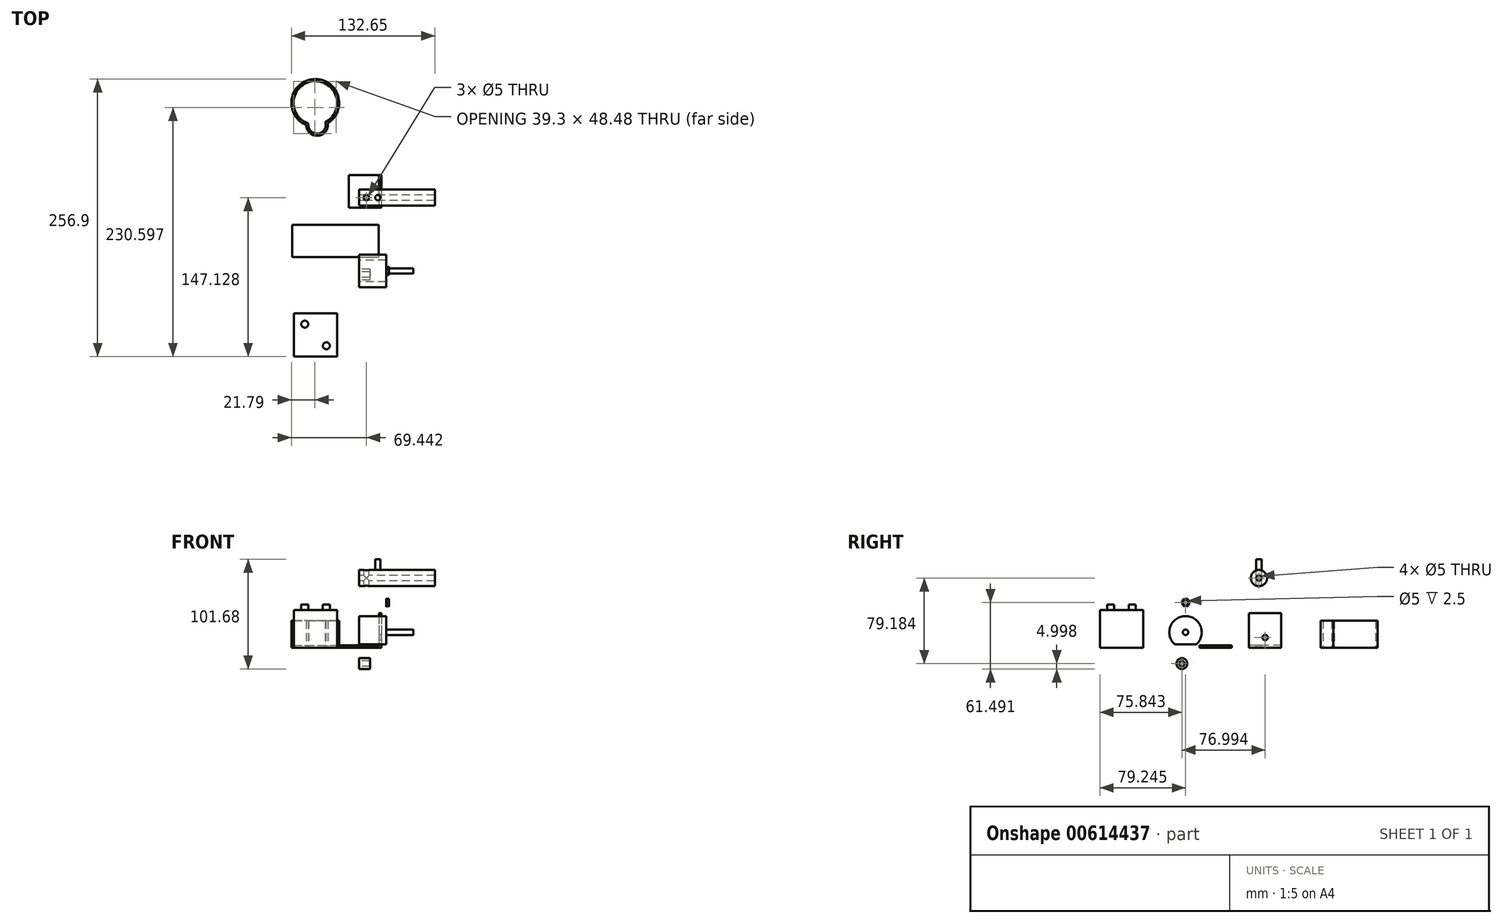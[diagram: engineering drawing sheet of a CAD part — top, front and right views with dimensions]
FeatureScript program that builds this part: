
annotation { "Feature Type Name" : "Feature", "Feature Type Description" : "" }
export const myFeature = defineFeature(function(context is Context, id is Id, definition is map)
    precondition{}
    {
        {
            var Q0;
            Q0=qCreatedBy(makeId("Top.planeOp"),FACE);
            var sketch = newSketch(context, id + "F0", { "sketchPlane" : qUnion([Q0])});
            skLineSegment(sketch, "E0.bottom", {"start": v(-9.51, 45.78) * mm, "end": v(20.49, 45.78) * mm});
            skLineSegment(sketch, "E0.top", {"start": v(-9.51, 15.78) * mm, "end": v(20.49, 15.78) * mm});
            skLineSegment(sketch, "E0.left", {"start": v(-9.51, 45.78) * mm, "end": v(-9.51, 15.78) * mm});
            skLineSegment(sketch, "E0.right", {"start": v(20.49, 45.78) * mm, "end": v(20.49, 15.78) * mm});
            skLineSegment(sketch, "E1.bottom", {"start": v(-61.86, 0) * mm, "end": v(18.14, 0) * mm});
            skLineSegment(sketch, "E1.top", {"start": v(-61.86, -30) * mm, "end": v(18.14, -30) * mm});
            skLineSegment(sketch, "E1.left", {"start": v(-61.86, 0) * mm, "end": v(-61.86, -30) * mm});
            skLineSegment(sketch, "E1.right", {"start": v(18.14, 0) * mm, "end": v(18.14, -30) * mm});
            skArc(sketch, "E2", {"start": v(-48.93, 92.28) * mm, "mid": v(-38.15, 82.3) * mm, "end": v(-29.06, 93.85) * mm});
            skArc(sketch, "E3", {"start": v(-29.06, 93.85) * mm, "mid": v(-42.29, 134.77) * mm, "end": v(-48.93, 92.28) * mm});
            skArc(sketch, "E4", {"start": v(-31.36, 94.85) * mm, "mid": v(-42.13, 132.78) * mm, "end": v(-46.82, 93.63) * mm});
            skArc(sketch, "E5", {"start": v(-46.82, 93.63) * mm, "mid": v(-38.3, 84.3) * mm, "end": v(-31.36, 94.85) * mm});
            skLineSegment(sketch, "E6.bottom", {"start": v(-60.3, -82.06) * mm, "end": v(-20.3, -82.06) * mm});
            skLineSegment(sketch, "E6.top", {"start": v(-60.3, -122.06) * mm, "end": v(-20.3, -122.06) * mm});
            skLineSegment(sketch, "E6.left", {"start": v(-60.3, -82.06) * mm, "end": v(-60.3, -122.06) * mm});
            skLineSegment(sketch, "E6.right", {"start": v(-20.3, -82.06) * mm, "end": v(-20.3, -122.06) * mm});
            skSolve(sketch);
        }
        {
            var Q0;
            Q0=makeQuery(id+"F0.imprint","IMPRINT",FACE,{"disambiguationData":[TD([[makeQuery(id+"F0.imprint","IMPRINT",EDGE,{"derivedFrom":sQuery(id+"F0.wireOp",EDGE,"E0.bottom")}),-1.0]])]});
            extrude(context, id + "F1", {"entities" : qUnion([Q0]), "depth" : 2 * mm, "offsetDistance" : 25 * mm});
        }
        {
            var Q0;
            Q0=makeQuery(id+"F1.opExtrude","CAP_FACE",FACE,{"disambiguationData":[OSD([sQuery(id+"F0.wireOp",EDGE,"E0.bottom"),sQuery(id+"F0.wireOp",EDGE,"E0.top"),sQuery(id+"F0.wireOp",EDGE,"E0.left"),sQuery(id+"F0.wireOp",EDGE,"E0.right")])],"isStart":false});
            var sketch = newSketch(context, id + "F2", { "sketchPlane" : qUnion([Q0])});
            skLineSegment(sketch, "E7", {"start": v(18.49, 45.78) * mm, "end": v(18.49, 15.78) * mm});
            skSolve(sketch);
        }
        {
            var Q0;
            {var subQ0=sQuery(id+"F2.wireOp",EDGE,"E7");Q0=makeQuery(id+"F2.imprint","IMPRINT",FACE,{"disambiguationData":[TD([[makeQuery(id+"F2.imprint","IMPRINT",EDGE,{"derivedFrom":subQ0}),1.0]])]});}
            extrude(context, id + "F3", {"entities" : qUnion([Q0]), "operationType" : NewBodyOperationType.ADD, "depth" : 30 * mm, "offsetDistance" : 25 * mm});
        }
        {
            var Q0;
            Q0=qCreatedBy(makeId("Right.planeOp"),FACE);
            var sketch = newSketch(context, id + "F4", { "sketchPlane" : qUnion([Q0])});
            skArc(sketch, "E8", {"start": v(-32.74, 3.14) * mm, "mid": v(-42.82, 29.25) * mm, "end": v(-52.9, 3.14) * mm});
            skLineSegment(sketch, "E9", {"start": v(-52.9, 3.14) * mm, "end": v(-32.74, 3.14) * mm});
            skCircle(sketch, "E10", {"center": v(-46.22, -14.73) * mm, "radius": 2.5 * mm});
            skCircle(sketch, "E11", {"center": v(-46.22, -14.73) * mm, "radius": 5 * mm});
            skCircle(sketch, "E12", {"center": v(-15.18, -14.73) * mm, "radius": 2.5 * mm});
            skCircle(sketch, "E13", {"center": v(-15.18, -14.73) * mm, "radius": 3.75 * mm});
            skSolve(sketch);
        }
        {
            var Q0;
            Q0=makeQuery(id+"F4.imprint","IMPRINT",FACE,{"disambiguationData":[TD([[makeQuery(id+"F4.imprint","IMPRINT",EDGE,{"derivedFrom":sQuery(id+"F4.wireOp",EDGE,"E8")}),1.0]])]});
            extrude(context, id + "F5", {"entities" : qUnion([Q0]), "depth" : 25 * mm, "offsetDistance" : 25 * mm});
        }
        {
            var Q0;
            Q0=makeQuery(id+"F5.opExtrude","CAP_FACE",FACE,{"disambiguationData":[OSD([sQuery(id+"F4.wireOp",EDGE,"E8"),sQuery(id+"F4.wireOp",EDGE,"E9")])],"isStart":false});
            var sketch = newSketch(context, id + "F6", { "sketchPlane" : qUnion([Q0])});
            skCircle(sketch, "E14", {"center": v(-42.82, 14.25) * mm, "radius": 2.5 * mm});
            skArc(sketch, "E15", {"start": v(-41.34, 45.21) * mm, "mid": v(-41.43, 45.25) * mm, "end": v(-41.52, 45.28) * mm});
            skCircle(sketch, "E16", {"center": v(-42.82, 41.76) * mm, "radius": 2.5 * mm});
            skCircle(sketch, "E17.cCircle", {"center": v(-42.82, 41.76) * mm, "radius": 3.3 * mm, "construction": true});
            skLineSegment(sketch, "E17.0", {"start": v(-41.41, 45.3) * mm, "end": v(-39.05, 42.31) * mm});
            skLineSegment(sketch, "E17.1", {"start": v(-39.05, 42.31) * mm, "end": v(-40.46, 38.78) * mm});
            skLineSegment(sketch, "E17.2", {"start": v(-40.46, 38.78) * mm, "end": v(-44.22, 38.23) * mm});
            skLineSegment(sketch, "E17.3", {"start": v(-44.22, 38.23) * mm, "end": v(-46.58, 41.21) * mm});
            skLineSegment(sketch, "E17.4", {"start": v(-46.58, 41.21) * mm, "end": v(-45.17, 44.74) * mm});
            skLineSegment(sketch, "E17.5", {"start": v(-45.17, 44.74) * mm, "end": v(-41.41, 45.3) * mm});
            skPoint(sketch, "E17.0.midPoint", {"position": v(-40.23, 43.8) * mm});
            skArc(sketch, "E18.trimOffspring", {"start": v(-39.1, 42.21) * mm, "mid": v(-39.1, 42.3) * mm, "end": v(-39.12, 42.4) * mm});
            skArc(sketch, "E19.trimOffspring", {"start": v(-45.07, 44.76) * mm, "mid": v(-45.14, 44.7) * mm, "end": v(-45.21, 44.65) * mm});
            skArc(sketch, "E20.trimOffspring", {"start": v(-46.54, 41.31) * mm, "mid": v(-46.53, 41.22) * mm, "end": v(-46.51, 41.13) * mm});
            skArc(sketch, "E21.trimOffspring", {"start": v(-44.29, 38.31) * mm, "mid": v(-44.2, 38.28) * mm, "end": v(-44.12, 38.24) * mm});
            skArc(sketch, "E22.trimOffspring", {"start": v(-40.56, 38.76) * mm, "mid": v(-40.5, 38.82) * mm, "end": v(-40.42, 38.88) * mm});
            skSolve(sketch);
        }
        {
            var Q0;
            Q0=makeQuery(id+"F6.imprint","IMPRINT",FACE,{"disambiguationData":[TD([[makeQuery(id+"F6.imprint","IMPRINT",EDGE,{"derivedFrom":sQuery(id+"F6.wireOp",EDGE,"E14")}),1.0]])]});
            extrude(context, id + "F7", {"entities" : qUnion([Q0]), "operationType" : NewBodyOperationType.ADD, "depth" : 25 * mm, "offsetDistance" : 25 * mm});
        }
        {
            var Q0;
            Q0=makeQuery(id+"F3.opExtrude","SWEPT_FACE",FACE,{"disambiguationData":[OSD([sQuery(id+"F2.wireOp",EDGE,"E7")])]});
            var sketch = newSketch(context, id + "F8", { "sketchPlane" : qUnion([Q0])});
            skCircle(sketch, "E23", {"center": v(-30.78, 9.4) * mm, "radius": 2.5 * mm});
            skLineSegment(sketch, "E24", {"start": v(-45.28, 2) * mm, "end": v(-19.09, 2) * mm});
            skSolve(sketch);
        }
        {
            var Q0;
            Q0=makeQuery(id+"F8.imprint","IMPRINT",FACE,{"disambiguationData":[TD([[makeQuery(id+"F8.imprint","IMPRINT",EDGE,{"derivedFrom":sQuery(id+"F8.wireOp",EDGE,"E23")}),1.0]])]});
            extrude(context, id + "F9", {"entities" : qUnion([Q0]), "operationType" : NewBodyOperationType.REMOVE, "endBound" : BoundingType.UP_TO_NEXT, "oppositeDirection" : true, "depth" : 25 * mm, "offsetDistance" : 25 * mm});
        }
        {
            var Q0;
            {var subQ0=sQuery(id+"F0.wireOp",EDGE,"E1.left");Q0=makeQuery(id+"F0.imprint","IMPRINT",FACE,{"disambiguationData":[TD([[makeQuery(id+"F0.imprint","IMPRINT",EDGE,{"derivedFrom":subQ0}),1.0]])]});}
            var Q1;
            {var subQ0=sQuery(id+"F0.wireOp",EDGE,"5NgWmGHn-8wDg-qtu3-9MUL-ouu6PDl5EJlb");Q1=makeQuery(id+"F0.imprint","IMPRINT",FACE,{"disambiguationData":[TD([[makeQuery(id+"F0.imprint","IMPRINT",EDGE,{"derivedFrom":subQ0}),1.0]])]});}
            var Q2;
            {var subQ0=sQuery(id+"F0.wireOp",EDGE,"E1.right");Q2=makeQuery(id+"F0.imprint","IMPRINT",FACE,{"disambiguationData":[TD([[makeQuery(id+"F0.imprint","IMPRINT",EDGE,{"derivedFrom":subQ0}),-1.0]])]});}
            extrude(context, id + "F10", {"entities" : qUnion([Q0, Q1, Q2]), "depth" : 2 * mm, "offsetDistance" : 25 * mm});
        }
        {
            var Q0;
            Q0=makeQuery(id+"F10.opExtrude","CAP_FACE",FACE,{"disambiguationData":[OSD([sQuery(id+"F0.wireOp",EDGE,"E1.bottom"),sQuery(id+"F0.wireOp",EDGE,"E1.top"),sQuery(id+"F0.wireOp",EDGE,"E1.left"),sQuery(id+"F0.wireOp",EDGE,"E1.right")])],"isStart":false});
            var sketch = newSketch(context, id + "F11", { "sketchPlane" : qUnion([Q0])});
            skLineSegment(sketch, "E25", {"start": v(-31.86, 0) * mm, "end": v(-31.86, -30) * mm});
            skLineSegment(sketch, "E26", {"start": v(-11.86, 0) * mm, "end": v(-11.86, -30) * mm});
            skSolve(sketch);
        }
        {
            var Q0;
            Q0=makeQuery(id+"F6.imprint","IMPRINT",FACE,{"disambiguationData":[TD([[makeQuery(id+"F6.imprint","IMPRINT",EDGE,{"derivedFrom":sQuery(id+"F6.wireOp",EDGE,"E15")}),1.0]])]});
            extrude(context, id + "F12", {"entities" : qUnion([Q0]), "depth" : 2.5 * mm, "offsetDistance" : 25 * mm});
        }
        {
            var Q0;
            Q0=makeQuery(id+"F4.imprint","IMPRINT",FACE,{"disambiguationData":[TD([[makeQuery(id+"F4.imprint","IMPRINT",EDGE,{"derivedFrom":sQuery(id+"F4.wireOp",EDGE,"E10")}),-1.0]])]});
            extrude(context, id + "F13", {"entities" : qUnion([Q0]), "depth" : 10 * mm, "offsetDistance" : 25 * mm});
        }
        {
            var Q0;
            Q0=makeQuery(id+"F0.imprint","IMPRINT",FACE,{"disambiguationData":[TD([[makeQuery(id+"F0.imprint","IMPRINT",EDGE,{"derivedFrom":sQuery(id+"F0.wireOp",EDGE,"E2")}),1.0]])]});
            extrude(context, id + "F14", {"entities" : qUnion([Q0]), "depth" : 25 * mm, "offsetDistance" : 25 * mm});
        }
        {
            var Q0;
            Q0=makeQuery(id+"F0.imprint","IMPRINT",FACE,{"disambiguationData":[TD([[makeQuery(id+"F0.imprint","IMPRINT",EDGE,{"derivedFrom":sQuery(id+"F0.wireOp",EDGE,"E6.bottom")}),-1.0]])]});
            extrude(context, id + "F15", {"entities" : qUnion([Q0]), "depth" : 40 * mm, "offsetDistance" : 25 * mm});
        }
        {
            var Q0;
            Q0=makeQuery(id+"F15.opExtrude","CAP_FACE",FACE,{"disambiguationData":[OSD([sQuery(id+"F0.wireOp",EDGE,"E6.bottom"),sQuery(id+"F0.wireOp",EDGE,"E6.top"),sQuery(id+"F0.wireOp",EDGE,"E6.left"),sQuery(id+"F0.wireOp",EDGE,"E6.right")])],"isStart":false});
            var sketch = newSketch(context, id + "F16", { "sketchPlane" : qUnion([Q0])});
            skLineSegment(sketch, "E27", {"start": v(-40.3, -82.06) * mm, "end": v(-40.3, -122.06) * mm, "construction": true});
            skLineSegment(sketch, "E28", {"start": v(-60.3, -102.06) * mm, "end": v(-20.3, -102.06) * mm, "construction": true});
            skCircle(sketch, "E29", {"center": v(-30.3, -92.06) * mm, "radius": 3.23 * mm});
            skCircle(sketch, "E30.MirrorC", {"center": v(-50.3, -92.06) * mm, "radius": 3.23 * mm});
            skCircle(sketch, "E31.MirrorC", {"center": v(-50.3, -112.06) * mm, "radius": 3.23 * mm});
            skCircle(sketch, "E32.MirrorC", {"center": v(-30.3, -112.06) * mm, "radius": 3.23 * mm});
            skSolve(sketch);
        }
        {
            var Q0;
            Q0=makeQuery(id+"F16.imprint","IMPRINT",FACE,{"disambiguationData":[TD([[makeQuery(id+"F16.imprint","IMPRINT",EDGE,{"derivedFrom":sQuery(id+"F16.wireOp",EDGE,"E31.MirrorC")}),1.0]])]});
            var Q1;
            Q1=makeQuery(id+"F16.imprint","IMPRINT",FACE,{"disambiguationData":[TD([[makeQuery(id+"F16.imprint","IMPRINT",EDGE,{"derivedFrom":sQuery(id+"F16.wireOp",EDGE,"E32.MirrorC")}),-1.0]])]});
            var Q2;
            Q2=makeQuery(id+"F16.imprint","IMPRINT",FACE,{"disambiguationData":[TD([[makeQuery(id+"F16.imprint","IMPRINT",EDGE,{"derivedFrom":sQuery(id+"F16.wireOp",EDGE,"E29")}),1.0]])]});
            var Q3;
            Q3=makeQuery(id+"F16.imprint","IMPRINT",FACE,{"disambiguationData":[TD([[makeQuery(id+"F16.imprint","IMPRINT",EDGE,{"derivedFrom":sQuery(id+"F16.wireOp",EDGE,"E30.MirrorC")}),-1.0]])]});
            extrude(context, id + "F17", {"entities" : qUnion([Q0, Q1, Q2, Q3]), "operationType" : NewBodyOperationType.REMOVE, "oppositeDirection" : true, "depth" : 5 * mm, "offsetDistance" : 25 * mm});
        }
        {
            var Q0;
            Q0=qCreatedBy(makeId("Right.planeOp"),FACE);
            var sketch = newSketch(context, id + "F18", { "sketchPlane" : qUnion([Q0])});
            skCircle(sketch, "E33", {"center": v(25.07, 64.45) * mm, "radius": 7.5 * mm});
            skCircle(sketch, "E34", {"center": v(25.07, 64.45) * mm, "radius": 2.5 * mm});
            skLineSegment(sketch, "E35", {"start": v(25.07, 71.95) * mm, "end": v(37.6, 71.95) * mm});
            skLineSegment(sketch, "E36", {"start": v(25.07, 64.45) * mm, "end": v(25.07, 71.95) * mm, "construction": true});
            skLineSegment(sketch, "E37.MirrorCS", {"start": v(25.07, 71.95) * mm, "end": v(12.55, 71.95) * mm});
            skSolve(sketch);
        }
        {
            var Q0;
            Q0=makeQuery(id+"F18.imprint","IMPRINT",FACE,{"disambiguationData":[TD([[makeQuery(id+"F18.imprint","IMPRINT",EDGE,{"derivedFrom":sQuery(id+"F18.wireOp",EDGE,"E33")}),1.0]])]});
            extrude(context, id + "F19", {"entities" : qUnion([Q0]), "depth" : 70 * mm, "offsetDistance" : 25 * mm});
        }
        {
            var Q0;
            Q0=sQuery(id+"F18.wireOp",EDGE,"E35");
            var Q1;
            Q1=sQuery(id+"F18.wireOp",EDGE,"E37.MirrorCS");
            extrude(context, id + "F20", {"bodyType" : ToolBodyType.SURFACE, "surfaceEntities" : qUnion([Q0, Q1]), "depth" : 25 * mm, "offsetDistance" : 25 * mm});
        }
        {
            var Q0;
            Q0=makeQuery(id+"F20.opExtrude","SWEPT_FACE",FACE,{"disambiguationData":[OSD([sQuery(id+"F18.wireOp",EDGE,"E35")])]});
            var sketch = newSketch(context, id + "F21", { "sketchPlane" : qUnion([Q0])});
            skLineSegment(sketch, "E38", {"start": v(0, -25.07) * mm, "end": v(25, -25.07) * mm, "construction": true});
            skCircle(sketch, "E39", {"center": v(6.8, -25.07) * mm, "radius": 2.5 * mm});
            skCircle(sketch, "E40", {"center": v(17.32, -25.07) * mm, "radius": 2.5 * mm});
            skSolve(sketch);
        }
        {
            var Q0;
            Q0=makeQuery(id+"F21.imprint","IMPRINT",FACE,{"disambiguationData":[TD([[makeQuery(id+"F21.imprint","IMPRINT",EDGE,{"derivedFrom":sQuery(id+"F21.wireOp",EDGE,"E39")}),1.0]])]});
            extrude(context, id + "F22", {"entities" : qUnion([Q0]), "operationType" : NewBodyOperationType.REMOVE, "endBound" : BoundingType.THROUGH_ALL, "depth" : 25 * mm, "offsetDistance" : 25 * mm});
        }
        {
            var Q0;
            Q0=makeQuery(id+"F21.imprint","IMPRINT",FACE,{"disambiguationData":[TD([[makeQuery(id+"F21.imprint","IMPRINT",EDGE,{"derivedFrom":sQuery(id+"F21.wireOp",EDGE,"E40")}),1.0]])]});
            extrude(context, id + "F23", {"entities" : qUnion([Q0]), "oppositeDirection" : true, "depth" : 10 * mm, "offsetDistance" : 25 * mm});
        }
    });
